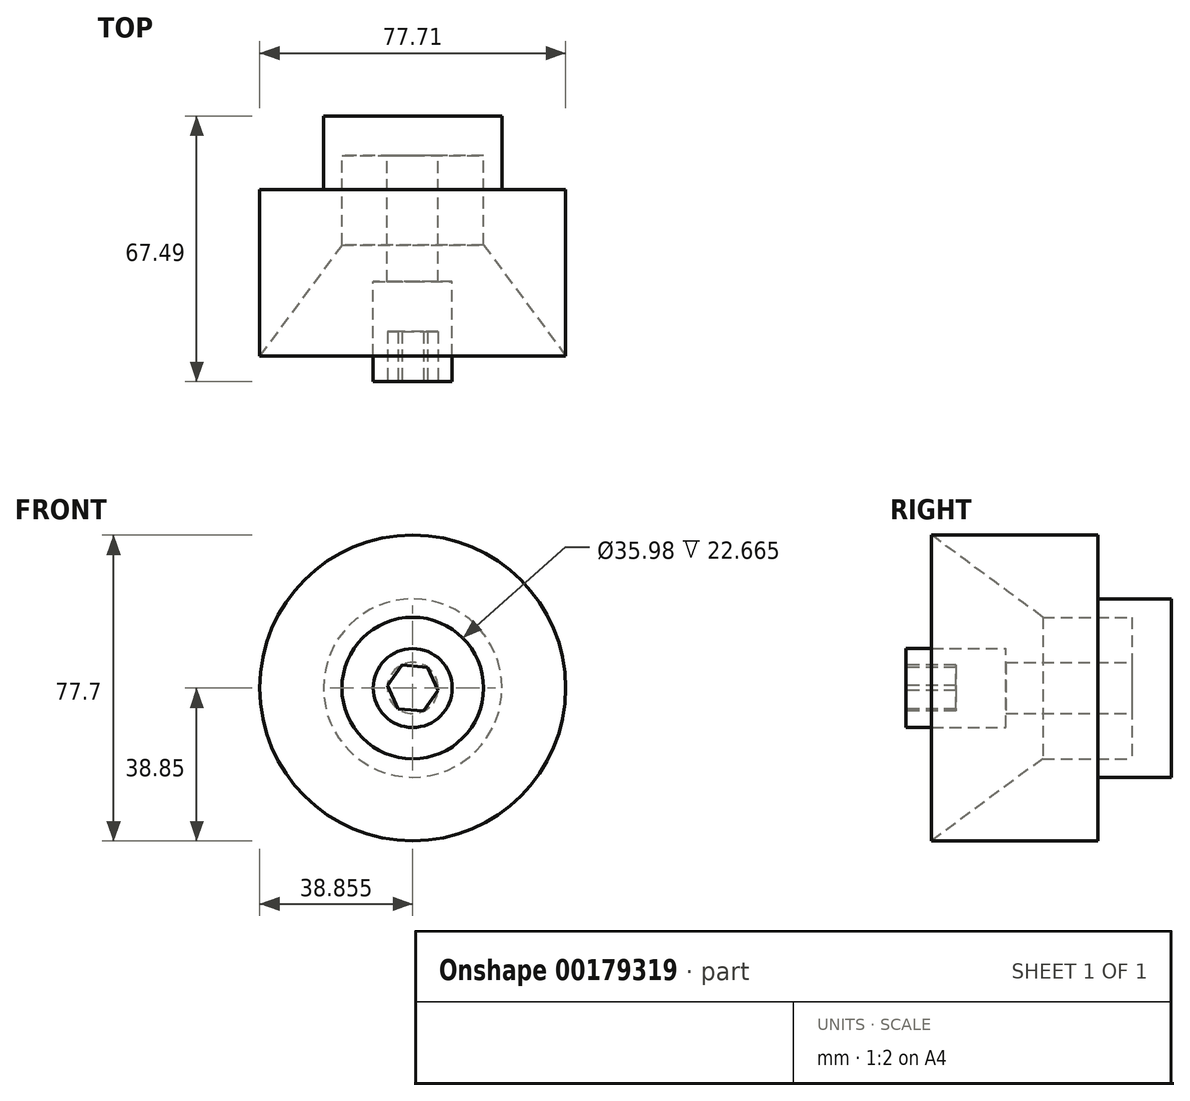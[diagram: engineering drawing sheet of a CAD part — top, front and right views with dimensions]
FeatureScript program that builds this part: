
annotation { "Feature Type Name" : "Feature", "Feature Type Description" : "" }
export const myFeature = defineFeature(function(context is Context, id is Id, definition is map)
    precondition{}
    {
        {
            var Q0;
            Q0=qCreatedBy(makeId("Top.planeOp"),FACE);
            var sketch = newSketch(context, id + "F0", { "sketchPlane" : qUnion([Q0])});
            skLineSegment(sketch, "E0", {"start": v(0, 0) * mm, "end": v(0, 42.27) * mm});
            skLineSegment(sketch, "E1", {"start": v(0, 42.27) * mm, "end": v(16.19, 42.27) * mm});
            skLineSegment(sketch, "E2", {"start": v(16.19, 42.27) * mm, "end": v(16.19, 60.98) * mm});
            skLineSegment(sketch, "E3", {"start": v(16.19, 60.98) * mm, "end": v(38.85, 60.98) * mm});
            skLineSegment(sketch, "E4", {"start": v(38.85, 60.98) * mm, "end": v(38.85, 18.89) * mm});
            skLineSegment(sketch, "E5", {"start": v(32.38, 18.89) * mm, "end": v(32.38, 50.9) * mm});
            skLineSegment(sketch, "E6", {"start": v(32.38, 50.9) * mm, "end": v(20.87, 50.9) * mm});
            skLineSegment(sketch, "E7", {"start": v(20.87, 50.9) * mm, "end": v(20.87, 28.24) * mm});
            skLineSegment(sketch, "E8", {"start": v(20.87, 28.24) * mm, "end": v(0, 0) * mm});
            skLineSegment(sketch, "E9", {"start": v(32.38, 18.89) * mm, "end": v(38.85, 18.89) * mm});
            skSolve(sketch);
        }
        {
            var Q0;
            Q0 = qSketchRegion(id + "F0", true);
            var Q1;
            Q1=sQuery(id+"F0.wireOp",EDGE,"E4");
            revolve(context, id + "F1", {"entities" : qUnion([Q0]), "axis" : qUnion([Q1]), "revolveType" : RevolveType.FULL});
        }
        {
            var Q0;
            Q0=makeQuery(id+"F1.opRevolve","SWEPT_FACE",FACE,{"disambiguationData":[OSD([sQuery(id+"F0.wireOp",EDGE,"E9")])]});
            var sketch = newSketch(context, id + "F2", { "sketchPlane" : qUnion([Q0])});
            skCircle(sketch, "E10", {"center": v(38.85, 0) * mm, "radius": 10.02 * mm});
            skSolve(sketch);
        }
        {
            var Q0;
            Q0 = qSketchRegion(id + "F2", true);
            extrude(context, id + "F3", {"entities" : qUnion([Q0]), "operationType" : NewBodyOperationType.ADD, "depth" : 25.4 * mm});
        }
        {
            var Q0;
            Q0=makeQuery(id+"F3.opExtrude","CAP_FACE",FACE,{"disambiguationData":[OSD([sQuery(id+"F2.wireOp",EDGE,"E10")])],"isStart":false});
            var sketch = newSketch(context, id + "F4", { "sketchPlane" : qUnion([Q0])});
            skCircle(sketch, "E11.cCircle", {"center": v(38.85, 0) * mm, "radius": 5.6 * mm, "construction": true});
            skLineSegment(sketch, "E11.0", {"start": v(35.12, -5.28) * mm, "end": v(32.42, 0.6) * mm});
            skLineSegment(sketch, "E11.1", {"start": v(32.42, 0.6) * mm, "end": v(36.15, 5.87) * mm});
            skLineSegment(sketch, "E11.2", {"start": v(36.15, 5.87) * mm, "end": v(42.6, 5.28) * mm});
            skLineSegment(sketch, "E11.3", {"start": v(42.6, 5.28) * mm, "end": v(45.3, -0.6) * mm});
            skLineSegment(sketch, "E11.4", {"start": v(45.3, -0.6) * mm, "end": v(41.55, -5.87) * mm});
            skLineSegment(sketch, "E11.5", {"start": v(41.55, -5.87) * mm, "end": v(35.12, -5.28) * mm});
            skPoint(sketch, "E11.0.midPoint", {"position": v(33.77, -2.34) * mm});
            skSolve(sketch);
        }
        {
            var Q0;
            Q0 = qSketchRegion(id + "F4", true);
            extrude(context, id + "F5", {"entities" : qUnion([Q0]), "operationType" : NewBodyOperationType.REMOVE, "oppositeDirection" : true, "depth" : 12.7 * mm});
        }
    });
